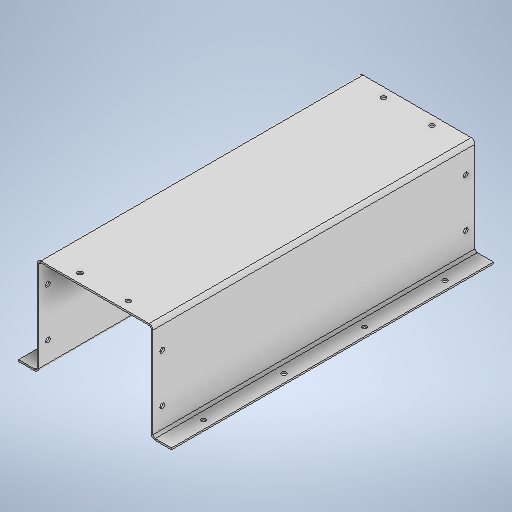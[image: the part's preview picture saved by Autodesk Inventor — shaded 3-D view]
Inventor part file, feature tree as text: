
AUTODESK INVENTOR PART (.ipt)
format: ipt  version: 2025 (Build 290162010, 162A)  size: 395,776 bytes
history: native  units: mm
features: sheet_metal_op x13, sketch x8, other x6, extrude x3, pattern_linear x1, mirror x1
ambient origin geometry x8: Origin, YZ Plane, XZ Plane, XY Plane, X Axis, Y Axis, Z Axis, Center Point
bodies: Solid1 (feature_tree)
feature tree (32):
  sheet_metal_op  "Face1"
  sheet_metal_op  "Flange1"
  sheet_metal_op  "Flange2"
  sheet_metal_op  "Flange3"
  sheet_metal_op  "Flange4"
  extrude  "Extrusion1"  Depth=400.0mm
  pattern_linear  "Rectangular Pattern2"  Count1=12  [1 undecoded]
  extrude  "Extrusion3"  Depth=2.75mm
  extrude  "Extrusion4"  Depth=2.75mm
  mirror  "Mirror2"
  sketch  "Sketch1"  dims[d0=140.0mm d1=400.0mm]
  other  "Plate1"
  sketch  "Sketch2"  dims[d2=2.0mm]
  other  "Plate2"
  sheet_metal_op  "Bend1"
  sheet_metal_op  "Corner1"
  sketch  "Sketch3"  dims[d3=2.0mm]
  other  "Plate3"
  sheet_metal_op  "Bend2"
  sheet_metal_op  "Corner2"
  sketch  "Sketch4"  dims[d4=1.0mm]
  other  "Plate4"
  sheet_metal_op  "Bend3"
  sheet_metal_op  "Corner3"
  sketch  "Sketch5"  dims[d5=4.0mm]
  other  "Plate5"
  sheet_metal_op  "Bend4"
  sheet_metal_op  "Corner4"
  sketch  "Sketch6"  dims[d6=2.75mm d7=120.0mm]
  sketch  "Sketch8"  dims[d8=90.0deg d9=2.75mm d10=8.0mm]
  sketch  "Sketch9"  dims[d11=2.0mm d12=2.75mm d13=2.0mm d14=1.0mm d15=4.0mm d16=2.75mm d17=120.0mm d18=90.0deg d19=2.75mm d20=8.0mm d21=2.0mm d22=2.75mm d23=2.0mm d24=1.0mm d25=4.0mm d26=2.75mm d27=25.0mm d28=90.0deg d29=2.75mm d30=8.0mm d31=2.0mm d32=2.75mm d33=2.0mm d34=1.0mm d35=4.0mm d36=2.75mm d37=25.0mm d38=90.0deg d39=2.75mm d40=8.0mm d41=2.0mm d42=2.75mm d43=6.0mm d44=50.0mm d45=0.0mm d46=0.0mm d60=40.0mm d62=100.0mm d63=20.0mm d65=169.75mm d68=6.0mm d69=60.0mm d70=0.0mm d71=0.0mm d72=6.0mm d73=11.5mm d74=37.3mm d76=0.0mm d77=0.0mm d78=30.0mm d79=11.5mm d80=60.0mm]
  other  "Definition1"
note: 1 required parameter value undecoded (feature->parameter linkage not recoverable at this tier; creation-order binding heuristic only, values carry confidence <= 0.55)
